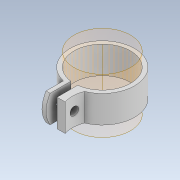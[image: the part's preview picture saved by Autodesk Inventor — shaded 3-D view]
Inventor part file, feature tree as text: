
AUTODESK INVENTOR PART (.ipt)
format: ipt  version: 2021 (Build 250183000, 183)  size: 175,616 bytes
history: native  units: mm
features: sketch x7, other x4, extrude x4, plane x1, mirror x1, split x1, revolve x1, hole x1
ambient origin geometry x8: Origin, YZ Plane, XZ Plane, XY Plane, X Axis, Y Axis, Z Axis, Center Point
bodies: Body1 (feature_tree), Body2 (feature_tree)
feature tree (20):
  other  "Sólido1"
  plane  "Plano de trabajo1"
  sketch  "Boceto3"  dims[d3=2.5mm d4=20.0mm]
  extrude  "Extrusión1"  Depth=40.0mm TaperAngle=0.0deg
  mirror  "Simetría1"
  split  "Dividir2"
  other  "Eje de trabajo1"
  revolve  "Revolución1"  [1 undecoded]
  extrude  "Extrusión2"  Depth=3.0mm TaperAngle=0.0deg
  extrude  "Extrusión3"  Depth=15.0mm
  extrude  "Extrusión4"  TaperAngle=90.0deg  [1 undecoded]
  hole  "Agujero3"  [1 undecoded]
  sketch  "Boceto1"  dims[d0=41.275mm d1=40.0mm d2=0.0mm]
  other  "Sup1"
  sketch  "Boceto5"  dims[d8=10.0mm d10=3.0mm d11=0.0mm]
  sketch  "Boceto6"  dims[d19=23.0mm d20=15.0mm]
  sketch  "Boceto8"  dims[d29=3.0mm d30=90.0deg]
  sketch  "Boceto9"  dims[d31=0.0mm d32=0.0mm d33=6.0mm]
  sketch  "Boceto10"  dims[d34=25.0mm d35=10.0mm d36=0.0mm d37=5.0mm d38=0.0mm d39=0.0mm d40=6.0mm d41=6.0mm d42=4.0mm d43=2.0mm d44=90.0deg d45=8.0mm d46=20.594885mm d47=7.5mm]
  other  "SuperficieExtrusión1"
note: 3 required parameter values undecoded (feature->parameter linkage not recoverable at this tier; creation-order binding heuristic only, values carry confidence <= 0.55)